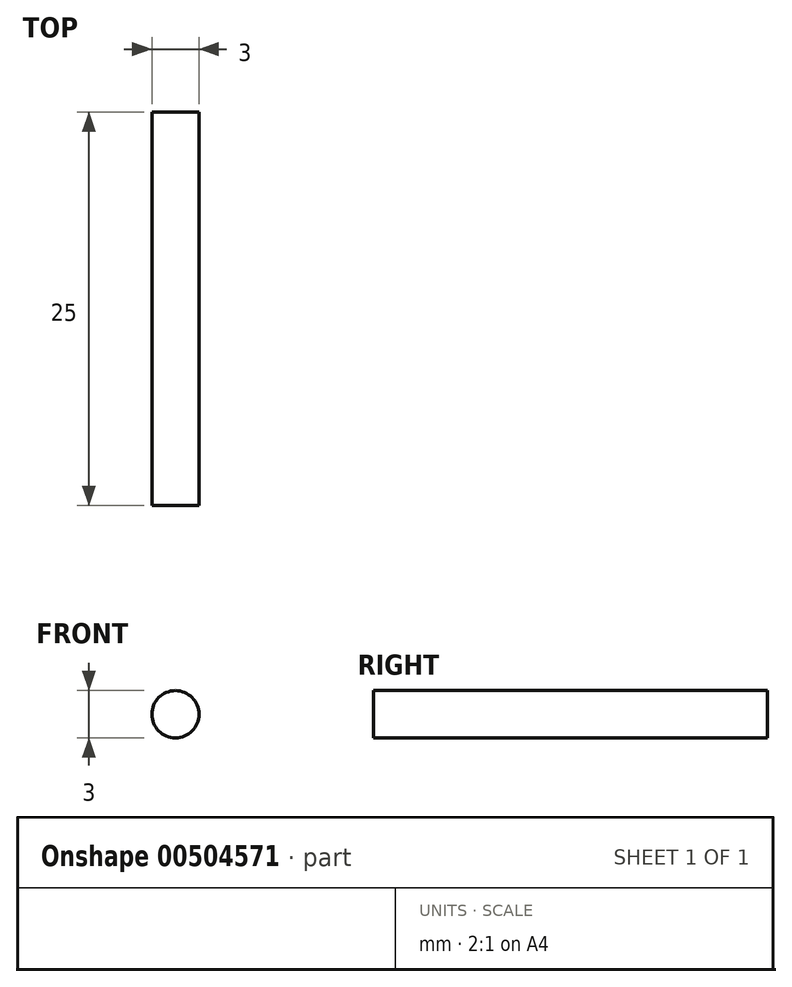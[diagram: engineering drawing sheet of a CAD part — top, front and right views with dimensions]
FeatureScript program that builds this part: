
annotation { "Feature Type Name" : "Feature", "Feature Type Description" : "" }
export const myFeature = defineFeature(function(context is Context, id is Id, definition is map)
    precondition{}
    {
        {
            var Q0;
            Q0=qCreatedBy(makeId("Front.planeOp"),FACE);
            var sketch = newSketch(context, id + "F0", { "sketchPlane" : qUnion([Q0])});
            skCircle(sketch, "E0", {"center": v(0, 0) * mm, "radius": 1.5 * mm});
            skSolve(sketch);
        }
        {
            var Q0;
            Q0=makeQuery(id+"F0.imprint","IMPRINT",FACE,{"disambiguationData":[TD([[makeQuery(id+"F0.imprint","IMPRINT",EDGE,{"derivedFrom":sQuery(id+"F0.wireOp",EDGE,"E0")}),1.0]])]});
            extrude(context, id + "F1", {"entities" : qUnion([Q0]), "depth" : 25 * mm, "offsetDistance" : 25 * mm});
        }
    });
